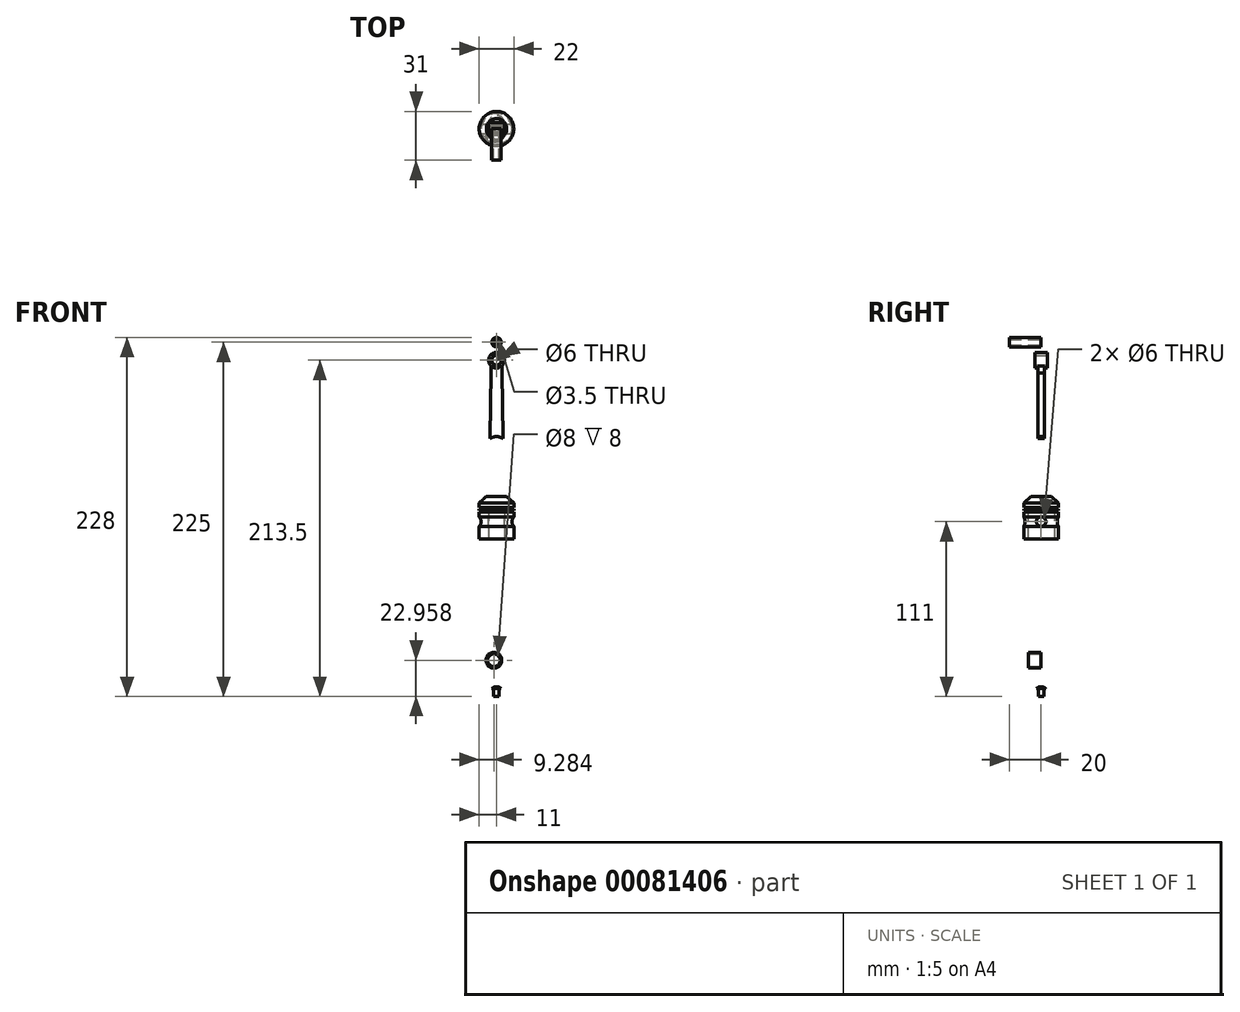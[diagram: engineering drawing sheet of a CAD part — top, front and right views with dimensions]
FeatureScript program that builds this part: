
annotation { "Feature Type Name" : "Feature", "Feature Type Description" : "" }
export const myFeature = defineFeature(function(context is Context, id is Id, definition is map)
    precondition{}
    {
        {
            var Q0;
            Q0=qCreatedBy(makeId("Front.planeOp"),FACE);
            var sketch = newSketch(context, id + "F0", { "sketchPlane" : qUnion([Q0])});
            skLineSegment(sketch, "E0", {"start": v(0, 0) * mm, "end": v(11, 0) * mm});
            skLineSegment(sketch, "E1", {"start": v(11, 0) * mm, "end": v(11, 8) * mm});
            skLineSegment(sketch, "E2", {"start": v(11, 8) * mm, "end": v(0, 8) * mm});
            skLineSegment(sketch, "E3", {"start": v(0, 0) * mm, "end": v(0, 14) * mm});
            skLineSegment(sketch, "E4", {"start": v(0, 14) * mm, "end": v(11, 14) * mm});
            skLineSegment(sketch, "E5", {"start": v(0, 0) * mm, "end": v(0, 17) * mm});
            skPoint(sketch, "E5.endSnap0", {"position": v(0, 7) * mm});
            skLineSegment(sketch, "E6", {"start": v(0, 17) * mm, "end": v(11, 17) * mm});
            skLineSegment(sketch, "E7", {"start": v(11, 17) * mm, "end": v(11, 14) * mm});
            skLineSegment(sketch, "E8", {"start": v(0, 0) * mm, "end": v(0, 18) * mm});
            skLineSegment(sketch, "E9", {"start": v(0, 18) * mm, "end": v(11, 18) * mm});
            skLineSegment(sketch, "E10", {"start": v(11, 18) * mm, "end": v(11, 19) * mm});
            skLineSegment(sketch, "E11", {"start": v(11, 19) * mm, "end": v(0, 19) * mm});
            skLineSegment(sketch, "E12", {"start": v(0, 19) * mm, "end": v(0, 18) * mm});
            skLineSegment(sketch, "E13", {"start": v(0, 17) * mm, "end": v(9.75, 17) * mm});
            skLineSegment(sketch, "E14", {"start": v(9.75, 17) * mm, "end": v(9.75, 18) * mm});
            skLineSegment(sketch, "E15", {"start": v(9.75, 18) * mm, "end": v(9.75, 19) * mm});
            skLineSegment(sketch, "E16", {"start": v(9.75, 19) * mm, "end": v(9.75, 20) * mm});
            skLineSegment(sketch, "E17", {"start": v(9.75, 20) * mm, "end": v(11, 20) * mm});
            skLineSegment(sketch, "E18", {"start": v(0, 0) * mm, "end": v(0, 23) * mm});
            skLineSegment(sketch, "E19", {"start": v(0, 23) * mm, "end": v(11, 23) * mm});
            skLineSegment(sketch, "E20", {"start": v(11, 23) * mm, "end": v(11, 20) * mm});
            skLineSegment(sketch, "E21", {"start": v(0, 0) * mm, "end": v(0, 27) * mm});
            skLineSegment(sketch, "E22", {"start": v(0, 27) * mm, "end": v(6.5, 27) * mm});
            skLineSegment(sketch, "E23", {"start": v(6.5, 27) * mm, "end": v(11, 23) * mm});
            skArc(sketch, "E24", {"start": v(11, 14) * mm, "mid": v(10.25, 11) * mm, "end": v(11, 8) * mm});
            skSolve(sketch);
        }
        {
            var Q0;
            Q0 = qSketchRegion(id + "F0", true);
            var Q1;
            Q1=sQuery(id+"F0.wireOp",EDGE,"E21");
            revolve(context, id + "F1", {"entities" : qUnion([Q0]), "axis" : qUnion([Q1]), "revolveType" : RevolveType.FULL});
        }
        {
            var Q0;
            Q0=qCreatedBy(makeId("Right.planeOp"),FACE);
            var sketch = newSketch(context, id + "F2", { "sketchPlane" : qUnion([Q0])});
            skLineSegment(sketch, "E25", {"start": v(0, 0) * mm, "end": v(0, 11) * mm});
            skCircle(sketch, "E26", {"center": v(0, 11) * mm, "radius": 3 * mm});
            skSolve(sketch);
        }
        {
            var Q0;
            Q0 = qSketchRegion(id + "F2", true);
            extrude(context, id + "F3", {"entities" : qUnion([Q0]), "operationType" : NewBodyOperationType.REMOVE, "endBound" : BoundingType.SYMMETRIC, "oppositeDirection" : true, "depth" : 25 * mm});
        }
        {
            var Q0;
            Q0=makeQuery(id+"F1.opRevolve","SWEPT_FACE",FACE,{"disambiguationData":[OSD([sQuery(id+"F0.wireOp",EDGE,"E0")])]});
            var sketch = newSketch(context, id + "F4", { "sketchPlane" : qUnion([Q0])});
            skLineSegment(sketch, "E27", {"start": v(0, 0) * mm, "end": v(0, 3.5) * mm});
            skLineSegment(sketch, "E28", {"start": v(0, 0) * mm, "end": v(5, 0) * mm});
            skLineSegment(sketch, "E29", {"start": v(5, 0) * mm, "end": v(5, 3.5) * mm});
            skArc(sketch, "E30", {"start": v(5, 3.5) * mm, "mid": v(0, 8.5) * mm, "end": v(-5, 3.5) * mm});
            skArc(sketch, "E31.MirrorC", {"start": v(5, -3.5) * mm, "mid": v(0, -8.5) * mm, "end": v(-5, -3.5) * mm});
            skLineSegment(sketch, "E32", {"start": v(5, -3.5) * mm, "end": v(5, 3.5) * mm});
            skLineSegment(sketch, "E33.MirrorCS", {"start": v(-5, -3.5) * mm, "end": v(-5, 3.5) * mm});
            skSolve(sketch);
        }
        {
            var Q0;
            Q0 = qSketchRegion(id + "F4", true);
            extrude(context, id + "F5", {"entities" : qUnion([Q0]), "operationType" : NewBodyOperationType.REMOVE, "oppositeDirection" : true, "depth" : 19 * mm});
        }
        {
            var Q0;
            Q0=makeQuery(id+"F1.opRevolve","SWEPT_BODY",BODY,{"disambiguationData":[OSD([sQuery(id+"F0.wireOp",EDGE,"E0"),sQuery(id+"F0.wireOp",EDGE,"E1"),sQuery(id+"F0.wireOp",EDGE,"E6"),sQuery(id+"F0.wireOp",EDGE,"E7"),sQuery(id+"F0.wireOp",EDGE,"E9"),sQuery(id+"F0.wireOp",EDGE,"E10"),sQuery(id+"F0.wireOp",EDGE,"E11"),sQuery(id+"F0.wireOp",EDGE,"E14"),sQuery(id+"F0.wireOp",EDGE,"E16"),sQuery(id+"F0.wireOp",EDGE,"E17"),sQuery(id+"F0.wireOp",EDGE,"E20"),sQuery(id+"F0.wireOp",EDGE,"E21"),sQuery(id+"F0.wireOp",EDGE,"E22"),sQuery(id+"F0.wireOp",EDGE,"E23"),sQuery(id+"F0.wireOp",EDGE,"E24")])]});
            transform(context, id + "F6", {"entities" : qUnion([Q0]), "transformType" : TransformType.TRANSLATION_3D, "dx" : 0 * mm, "dy" : 0 * mm, "dz" : 100 * mm, "makeCopy" : false});
        }
        {
            var Q0;
            Q0=qCreatedBy(makeId("Front.planeOp"),FACE);
            var sketch = newSketch(context, id + "F7", { "sketchPlane" : qUnion([Q0])});
            skLineSegment(sketch, "E34", {"start": v(0, 0) * mm, "end": v(0, 68.5) * mm});
            skLineSegment(sketch, "E35", {"start": v(0, 68.5) * mm, "end": v(0, 63.5) * mm});
            skCircle(sketch, "E36", {"center": v(0, 63.5) * mm, "radius": 5 * mm});
            skCircle(sketch, "E37", {"center": v(0, 63.5) * mm, "radius": 3 * mm});
            skLineSegment(sketch, "E38", {"start": v(0, 0) * mm, "end": v(0, 7.5) * mm});
            skCircle(sketch, "E39", {"center": v(0, 7.5) * mm, "radius": 7.5 * mm});
            skCircle(sketch, "E40", {"center": v(0, 7.5) * mm, "radius": 5 * mm});
            skLineSegment(sketch, "E41", {"start": v(0, 15) * mm, "end": v(4, 15) * mm});
            skLineSegment(sketch, "E42", {"start": v(4, 15) * mm, "end": v(3.56, 55.27) * mm});
            skLineSegment(sketch, "E43", {"start": v(3.56, 55.27) * mm, "end": v(3.56, 59.99) * mm});
            skLineSegment(sketch, "E44.MirrorCS", {"start": v(-3.56, 55.27) * mm, "end": v(-3.56, 59.99) * mm});
            skLineSegment(sketch, "E45.MirrorCS", {"start": v(-4, 15) * mm, "end": v(-3.56, 55.27) * mm});
            skLineSegment(sketch, "E46", {"start": v(-4, 15) * mm, "end": v(-4, 13.84) * mm});
            skLineSegment(sketch, "E47.MirrorCS", {"start": v(4, 15) * mm, "end": v(4, 13.84) * mm});
            skSolve(sketch);
        }
        {
            var Q0;
            {var subQ0=sQuery(id+"F7.wireOp",EDGE,"E44.MirrorCS");Q0=makeQuery(id+"F7.imprint","IMPRINT",FACE,{"disambiguationData":[TD([[makeQuery(id+"F7.imprint","IMPRINT",EDGE,{"derivedFrom":subQ0}),-1.0]])]});}
            var Q1;
            {var subQ0=sQuery(id+"F7.wireOp",EDGE,"E41");Q1=makeQuery(id+"F7.imprint","IMPRINT",FACE,{"disambiguationData":[TD([[makeQuery(id+"F7.imprint","IMPRINT",EDGE,{"derivedFrom":subQ0}),1.0]])]});}
            var Q2;
            {var subQ0=sQuery(id+"F7.wireOp",EDGE,"E41");Q2=makeQuery(id+"F7.imprint","IMPRINT",FACE,{"disambiguationData":[TD([[makeQuery(id+"F7.imprint","IMPRINT",EDGE,{"derivedFrom":subQ0}),-1.0]])]});}
            extrude(context, id + "F8", {"entities" : qUnion([Q0, Q1, Q2]), "endBound" : BoundingType.SYMMETRIC, "depth" : 4 * mm});
        }
        {
            var Q0;
            {var subQ0=sQuery(id+"F7.wireOp",EDGE,"E36");var subQ2=sQuery(id+"F7.wireOp",EDGE,"E34");var subQ3=makeQuery(id+"F7.imprint","INTERSECT",VERTEX,{"derivedFrom":[subQ2,subQ0]});Q0=makeQuery(id+"F7.imprint","IMPRINT",FACE,{"disambiguationData":[TD([[makeQuery(id+"F7.imprint","IMPRINT",EDGE,{"disambiguationData":[TD([[subQ3,-1.0]])],"derivedFrom":subQ2}),1.0]])]});}
            var Q1;
            {var subQ0=sQuery(id+"F7.wireOp",EDGE,"E36");var subQ4=sQuery(id+"F7.wireOp",EDGE,"E34");var subQ5=makeQuery(id+"F7.imprint","INTERSECT",VERTEX,{"derivedFrom":[subQ4,subQ0]});Q1=makeQuery(id+"F7.imprint","IMPRINT",FACE,{"disambiguationData":[TD([[makeQuery(id+"F7.imprint","IMPRINT",EDGE,{"disambiguationData":[TD([[subQ5,-1.0]])],"derivedFrom":subQ4}),-1.0]])]});}
            var Q2;
            {var subQ0=sQuery(id+"F7.wireOp",EDGE,"E39");var subQ4=sQuery(id+"F7.wireOp",EDGE,"E38");var subQ5=makeQuery(id+"F7.imprint","INTERSECT",VERTEX,{"derivedFrom":[subQ4,subQ0]});Q2=makeQuery(id+"F7.imprint","IMPRINT",FACE,{"disambiguationData":[TD([[makeQuery(id+"F7.imprint","IMPRINT",EDGE,{"disambiguationData":[TD([[subQ5,-1.0]])],"derivedFrom":subQ4}),-1.0]])]});}
            var Q3;
            {var subQ0=sQuery(id+"F7.wireOp",EDGE,"E39");var subQ1=sQuery(id+"F7.wireOp",EDGE,"E38");var subQ2=makeQuery(id+"F7.imprint","INTERSECT",VERTEX,{"derivedFrom":[subQ1,subQ0]});Q3=makeQuery(id+"F7.imprint","IMPRINT",FACE,{"disambiguationData":[TD([[makeQuery(id+"F7.imprint","IMPRINT",EDGE,{"disambiguationData":[TD([[subQ2,-1.0]])],"derivedFrom":subQ1}),1.0]])]});}
            extrude(context, id + "F9", {"entities" : qUnion([Q0, Q1, Q2, Q3]), "operationType" : NewBodyOperationType.ADD, "endBound" : BoundingType.SYMMETRIC, "depth" : 8 * mm});
        }
        {
            var Q0;
            Q0=makeQuery(id+"F8.opExtrude","SWEPT_BODY",BODY,{"disambiguationData":[OSD([sQuery(id+"F7.wireOp",EDGE,"E36"),sQuery(id+"F7.wireOp",EDGE,"E39"),sQuery(id+"F7.wireOp",EDGE,"E42"),sQuery(id+"F7.wireOp",EDGE,"E43"),sQuery(id+"F7.wireOp",EDGE,"E44.MirrorCS"),sQuery(id+"F7.wireOp",EDGE,"E45.MirrorCS"),sQuery(id+"F7.wireOp",EDGE,"E46"),sQuery(id+"F7.wireOp",EDGE,"E47.MirrorCS")])]});
            transform(context, id + "F10", {"entities" : qUnion([Q0]), "transformType" : TransformType.TRANSLATION_3D, "dx" : 0 * mm, "dy" : 0 * mm, "dz" : 150 * mm, "makeCopy" : false});
        }
        {
            var Q0;
            Q0=qCreatedBy(makeId("Front.planeOp"),FACE);
            var sketch = newSketch(context, id + "F11", { "sketchPlane" : qUnion([Q0])});
            skCircle(sketch, "E48", {"center": v(0, 0) * mm, "radius": 3 * mm});
            skCircle(sketch, "E49", {"center": v(0, 0) * mm, "radius": 1.75 * mm});
            skSolve(sketch);
        }
        {
            var Q0;
            Q0 = qSketchRegion(id + "F11", true);
            extrude(context, id + "F12", {"entities" : qUnion([Q0]), "depth" : 20 * mm});
        }
        {
            var Q0;
            Q0=makeQuery(id+"F12.opExtrude","SWEPT_BODY",BODY,{"disambiguationData":[OSD([sQuery(id+"F11.wireOp",EDGE,"E48"),sQuery(id+"F11.wireOp",EDGE,"E49")])]});
            transform(context, id + "F13", {"entities" : qUnion([Q0]), "transformType" : TransformType.TRANSLATION_3D, "dx" : 0 * mm, "dy" : 0 * mm, "dz" : 225 * mm, "makeCopy" : false});
        }
        {
            var Q0;
            Q0=qCreatedBy(makeId("Front.planeOp"),FACE);
            var sketch = newSketch(context, id + "F14", { "sketchPlane" : qUnion([Q0])});
            skLineSegment(sketch, "E50", {"start": v(0, 0) * mm, "end": v(1.75, 0) * mm});
            skLineSegment(sketch, "E51", {"start": v(1.75, 0) * mm, "end": v(1.75, 5) * mm});
            skLineSegment(sketch, "E52", {"start": v(0, 0) * mm, "end": v(0, 5) * mm});
            skLineSegment(sketch, "E53", {"start": v(1.75, 5) * mm, "end": v(3, 5) * mm});
            skLineSegment(sketch, "E54", {"start": v(3, 5) * mm, "end": v(1.75, 5) * mm});
            skArc(sketch, "E55", {"start": v(3, 5) * mm, "mid": v(1.6, 5.85) * mm, "end": v(0, 6.15) * mm});
            skLineSegment(sketch, "E56", {"start": v(0, 5) * mm, "end": v(0, 6.15) * mm});
            skSolve(sketch);
        }
        {
            var Q0;
            Q0 = qSketchRegion(id + "F14", true);
            var Q1;
            Q1=sQuery(id+"F14.wireOp",EDGE,"E52");
            revolve(context, id + "F15", {"entities" : qUnion([Q0]), "axis" : qUnion([Q1]), "revolveType" : RevolveType.FULL});
        }
        {
            var Q0;
            Q0=qCreatedBy(makeId("Front.planeOp"),FACE);
            var sketch = newSketch(context, id + "F16", { "sketchPlane" : qUnion([Q0])});
            skCircle(sketch, "E57", {"center": v(-1.72, 22.96) * mm, "radius": 5 * mm});
            skCircle(sketch, "E58", {"center": v(-1.72, 22.96) * mm, "radius": 4 * mm});
            skSolve(sketch);
        }
        {
            var Q0;
            Q0 = qSketchRegion(id + "F16", true);
            extrude(context, id + "F17", {"entities" : qUnion([Q0]), "depth" : 8 * mm});
        }
    });
